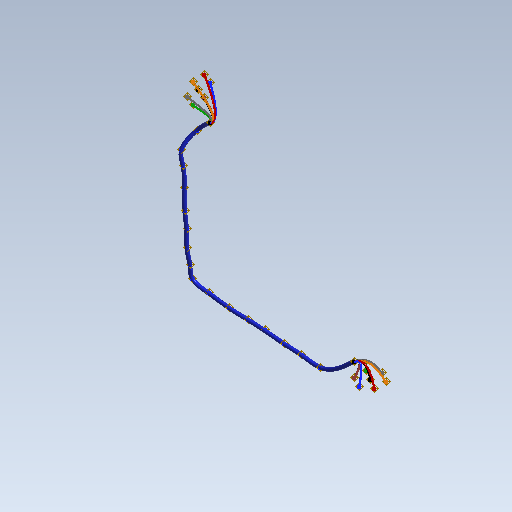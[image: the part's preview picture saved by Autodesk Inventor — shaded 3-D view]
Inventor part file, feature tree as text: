
AUTODESK INVENTOR PART (.ipt)
format: ipt  version: 2021 (Build 250183000, 183)  size: 855,552 bytes
history: native  units: mm (DEFAULTED — no unit token found)
features: other x92, sketch x15
bodies: Body1 (feature_tree), Body2 (feature_tree), Body3 (feature_tree), Body4 (feature_tree), Body5 (feature_tree), Body6 (feature_tree), Body7 (feature_tree), Body8 (feature_tree), Body9 (feature_tree), Body10 (feature_tree), Body11 (feature_tree), Body12 (feature_tree), Body13 (feature_tree), Body14 (feature_tree), Body15 (feature_tree)
feature tree (107):
  other  "Origem"
  other  "Ponto de trabalho1"
  other  "Ponto de trabalho2"
  other  "Fio1"
  other  "Ponto de trabalho3"
  other  "Ponto de trabalho4"
  other  "Fio2"
  other  "Ponto de trabalho5"
  other  "Ponto de trabalho6"
  other  "Fio3"
  other  "Ponto de trabalho7"
  other  "Ponto de trabalho8"
  other  "Fio4"
  other  "Ponto de trabalho9"
  other  "Ponto de trabalho10"
  other  "Fio5"
  other  "Ponto de trabalho11"
  other  "Ponto de trabalho12"
  other  "Fio6"
  other  "Ponto de trabalho13"
  other  "Ponto de trabalho14"
  other  "Fio7"
  other  "Ponto de trabalho15"
  other  "Ponto de trabalho16"
  other  "Segmento1"
  other  "Ponto de trabalho17"
  other  "Ponto de trabalho18"
  other  "Ponto de trabalho19"
  other  "Ponto de trabalho20"
  other  "Ponto de trabalho21"
  other  "Ponto de trabalho22"
  other  "Ponto de trabalho23"
  other  "Ponto de trabalho24"
  other  "Ponto de trabalho25"
  other  "Ponto de trabalho26"
  other  "Ponto de trabalho27"
  other  "Ponto de trabalho28"
  other  "Ponto de trabalho29"
  other  "Ponto de trabalho30"
  other  "Ponto de trabalho31"
  other  "Ponto de trabalho32"
  other  "Plano de trabalho1"
  other  "Plano de trabalho2"
  other  "Plano de trabalho3"
  other  "Plano de trabalho4"
  other  "Plano de trabalho5"
  other  "Plano de trabalho10"
  other  "Plano de trabalho11"
  other  "Plano de trabalho12"
  other  "Plano de trabalho13"
  other  "Plano de trabalho14"
  other  "Plano de trabalho15"
  other  "Plano de trabalho16"
  other  "Plano de trabalho17"
  other  "Plano de trabalho18"
  other  "Plano de trabalho19"
  other  "Plano YZ"
  other  "Plano XZ"
  other  "Plano XY"
  other  "Eixo X"
  other  "Eixo Y"
  other  "Eixo Z"
  sketch  "Esboço1"  dims[d0=0.0mm d1=0.0mm]
  other  "Sup1"
  sketch  "Esboço2"  dims[d2=0.0mm d3=0.0mm]
  other  "Sup2"
  sketch  "Esboço3"  dims[d4=0.0mm d5=0.0mm]
  other  "Sup3"
  sketch  "Esboço4"  dims[d6=0.0mm d7=0.0mm]
  other  "Sup4"
  sketch  "Esboço5"  dims[d8=0.0mm d9=0.0mm]
  other  "Sup5"
  sketch  "Esboço10"  dims[d12=0.0mm d13=0.0mm]
  other  "Sup7"
  sketch  "Esboço11"  dims[d14=0.0mm d15=0.0mm]
  other  "Sup8"
  sketch  "Esboço12"  dims[d16=0.0mm d17=0.0mm]
  other  "Sup9"
  sketch  "Esboço13"  dims[d18=0.0mm d19=0.0mm]
  other  "Sup10"
  sketch  "Esboço14"  dims[d20=0.0mm d21=0.0mm]
  other  "Sup11"
  sketch  "Esboço15"  dims[d22=0.0mm d23=0.0mm]
  other  "Sup12"
  sketch  "Esboço16"  dims[d24=0.0mm d25=0.0mm]
  other  "Sup13"
  sketch  "Esboço17"  dims[d26=0.0mm d27=0.0mm]
  other  "Sup14"
  sketch  "Esboço18"  dims[d28=0.0mm d29=0.0mm]
  other  "Sup15"
  sketch  "Esboço19"  dims[d30=0.0mm d31=0.0mm]
  other  "Sup16"
  other  "SuperfícieBarrido1"
  other  "SuperfícieBarrido2"
  other  "SuperfícieBarrido3"
  other  "SuperfícieBarrido4"
  other  "SuperfícieBarrido5"
  other  "SuperfícieBarrido7"
  other  "SuperfícieBarrido8"
  other  "SuperfícieBarrido9"
  other  "SuperfícieBarrido10"
  other  "SuperfícieBarrido11"
  other  "SuperfícieBarrido12"
  other  "SuperfícieBarrido13"
  other  "SuperfícieBarrido14"
  other  "SuperfícieBarrido15"
  other  "SuperfícieBarrido16"
